# Revit family: No interlocked sockets 480_500 V
name_source: partatom
category: Installations électriques
revit_build: Autodesk Revit 2018 (Build: 20170223_1515(x64)
units: mm (PartAtom-declared; Revit-internal decimal feet)

## family parameters
Conserver l'orientation des annotations = Non
Cote de connecteur circulaire = Utiliser le diamètre
Couper avec des vides une fois chargée = Non
Hôte = Face
Partagée = Non
Point de calcul de pièce = Non
Type d'élément = Normal

## types (6) — shared parameters
Elévation par défaut = 1000 mm  [stored 3.28084 ft]
Fabricant = Legrand
International standard socket for flush mounting or surface mounting with accessory allows the connection of power devices = International standard socket for flush mounting or surface mounting with accessory allows the connection of power devices
Maximum use temperature = 40
Minimum installation temperature = -5
Minimum use temperature = -25
Position of earth h = 7
Product family = 0854-P17 TEMPRA PRO
Standard IEC or NFC = IEC
Tension V = 500 V  50/60 Hz black
characteristic color = black
connecting type = screw terminals
material of box = plastic
resistance to chocks IK = 9

## per-type parameters (varying)
| type | Description | Flush E or Surface mounting S | Number of poles | depth for flush mounting mm | depth mm | halogen free | height mm | horizontal fixing distance mm | intensity A | protection class IP | vertical fixing distance mm | width mm |
| P17 - 63A - 3P+E - IP67 | LG-555592_Panelsocket 63A 3P+E 500V IP67 | flush mounting | 4 | 84 mm  [stored 0.275591 ft] | 161 mm  [stored 0.528215 ft] | Non | 106 mm  [stored 0.347769 ft] | 77 mm | 63 A |  | 85 mm | 106 mm  [stored 0.347769 ft] |
| P17 - 32A - 3P+E - IP67 | LG-555492_Panel mounting socket  32A 3P+E 480/500V IP67 | flush and surface mounting | 4 | 42 mm | 92 mm | Non | 84 mm  [stored 0.275591 ft] | 70 mm | 32 A |  | 70 mm | 84 mm  [stored 0.275591 ft] |
| P17 - 16A - 3P+E - IP67 | LG-555392_Panel mounting socket  P17 16A 3P+E 480/500V IP67 | flush and surface mounting | 4 | 36 mm | 79 mm | Non | 84 mm  [stored 0.275591 ft] | 70 mm | 16 A | IP44 | 70 mm | 84 mm  [stored 0.275591 ft] |
| P17 - 32A - 3P+E - IP44 | LG-555292_Panel mounting socket  P17  32A 3P+E 480/500V IP44 | flush and surface mounting | 4 | 42 mm | 87 mm | Oui | 84 mm  [stored 0.275591 ft] | 70 mm | 32 A |  | 70 mm | 84 mm  [stored 0.275591 ft] |
| P17 - 16A - 4P+E - IP44 | LG-555193_Panel mounting socket P17 16A 4P+E 480/500V IP44 | flush and surface mounting | 5 | 37 mm | 76 mm | Oui | 84 mm  [stored 0.275591 ft] | 70 mm | 16 A | IP44 | 70 mm | 84 mm  [stored 0.275591 ft] |
| P17 - 16A - 3P+E - IP44 | LG-555192_Panel mounting socket P17  16A 3P+E 480/500V IP44 | flush and surface mounting | 4 | 36 mm | 74 mm  [stored 0.242782 ft] | Oui | 84 mm  [stored 0.275591 ft] | 70 mm | 16 A | IP44 | 70 mm | 84 mm  [stored 0.275591 ft] |

note: [stored X ft] marks values corroborated as IEEE doubles in the binary element streams (Revit-internal decimal feet)
